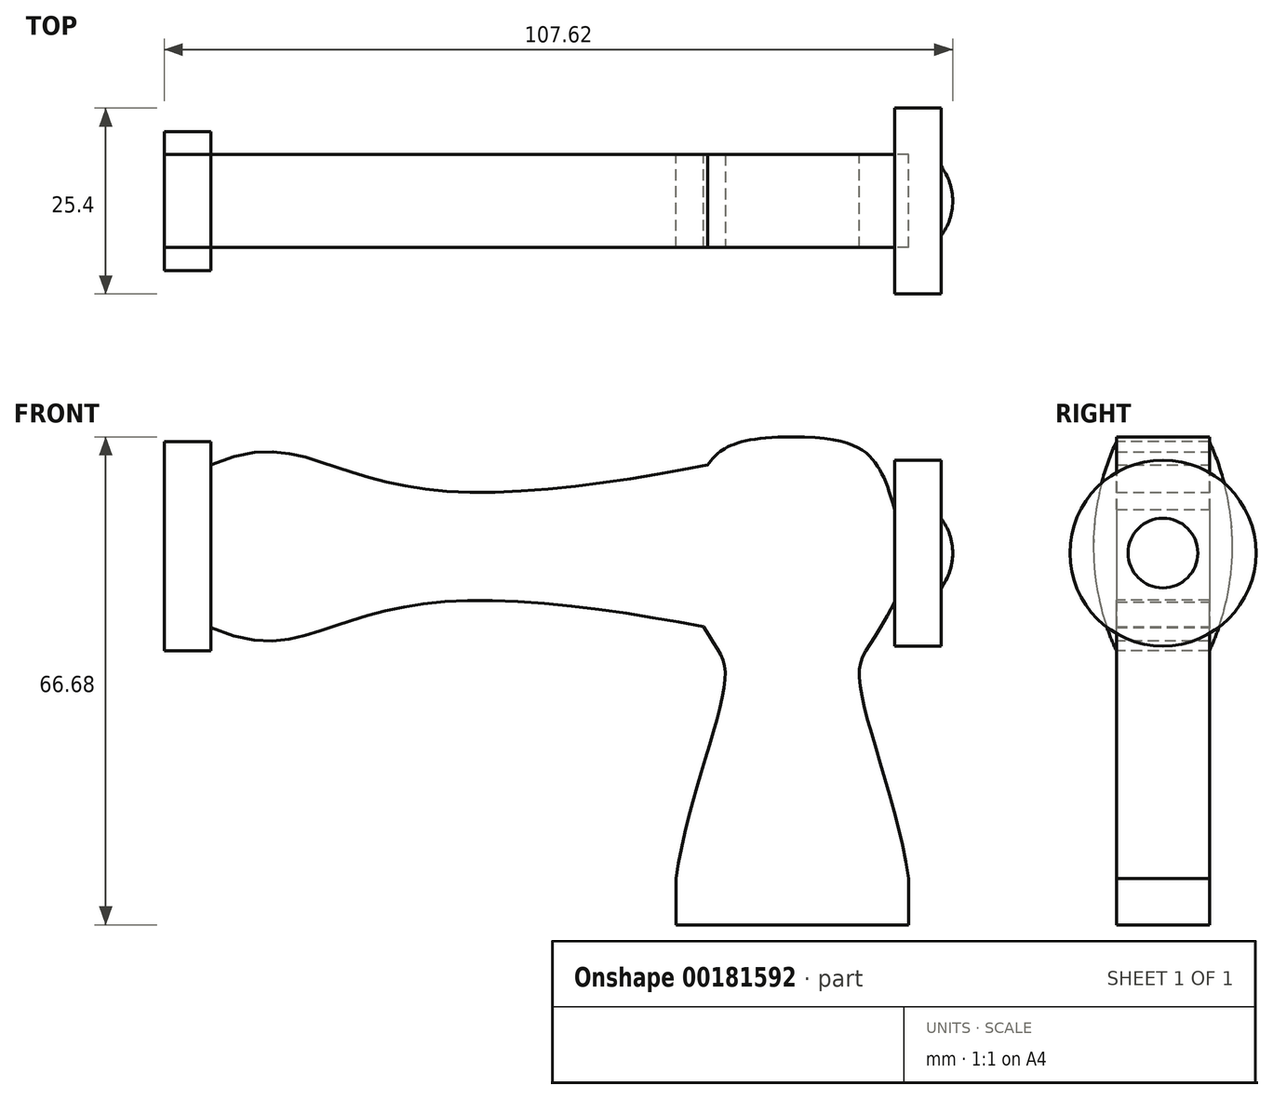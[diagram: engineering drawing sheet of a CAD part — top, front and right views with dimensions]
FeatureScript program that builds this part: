
annotation { "Feature Type Name" : "Feature", "Feature Type Description" : "" }
export const myFeature = defineFeature(function(context is Context, id is Id, definition is map)
    precondition{}
    {
        {
            var Q0;
            Q0=qCreatedBy(makeId("Front.planeOp"),FACE);
            var sketch = newSketch(context, id + "F0", { "sketchPlane" : qUnion([Q0])});
            skLineSegment(sketch, "E0", {"start": v(0, 63.34) * mm, "end": v(0, -25.62) * mm, "construction": true});
            skLineSegment(sketch, "E1", {"start": v(0, 0) * mm, "end": v(15.87, 0) * mm});
            skLineSegment(sketch, "E2", {"start": v(15.88, 0) * mm, "end": v(15.88, 6.35) * mm});
            skFitSpline(sketch, "E3", {"points": [v(15.88, 6.35) * mm, v(9.14, 34) * mm, v(14.67, 45.56) * mm], "startDerivative": vector(-7.68, 53.58) * mm, "endDerivative": vector(26.05, 56.21) * mm});
            skLineSegment(sketch, "E4", {"start": v(14.67, 45.56) * mm, "end": v(14.67, 53.82) * mm});
            skFitSpline(sketch, "E5", {"points": [v(14.67, 53.82) * mm, v(11.53, 62.83) * mm, v(0, 66.68) * mm], "startDerivative": vector(-6.78, 29.85) * mm, "endDerivative": vector(-44.66, 0) * mm});
            skFitSpline(sketch, "E6.MirrorCS", {"points": [v(-14.67, 53.82) * mm, v(-11.53, 62.83) * mm, v(0, 66.68) * mm], "startDerivative": vector(6.78, 29.85) * mm, "endDerivative": vector(44.66, 0) * mm});
            skFitSpline(sketch, "E7.MirrorCS", {"points": [v(-15.87, 6.35) * mm, v(-9.14, 34) * mm, v(-14.67, 45.56) * mm], "startDerivative": vector(7.68, 53.58) * mm, "endDerivative": vector(-26.05, 56.21) * mm});
            skLineSegment(sketch, "E8.MirrorCS", {"start": v(-15.87, 0) * mm, "end": v(-15.87, 6.35) * mm});
            skLineSegment(sketch, "E9.MirrorCS", {"start": v(0, 0) * mm, "end": v(-15.87, 0) * mm});
            skFitSpline(sketch, "E10", {"points": [v(-11.53, 62.83) * mm, v(-45.8, 59.16) * mm, v(-63.17, 62.83) * mm, v(-79.38, 62.83) * mm], "startDerivative": vector(-74.94, -14.82) * mm, "endDerivative": vector(-77.7, -33.1) * mm});
            skLineSegment(sketch, "E11", {"start": v(-90.87, 51.72) * mm, "end": v(5.33, 51.72) * mm, "construction": true});
            skFitSpline(sketch, "E12.MirrorCS", {"points": [v(-11.53, 40.6) * mm, v(-45.8, 44.27) * mm, v(-63.17, 40.6) * mm, v(-79.38, 40.6) * mm], "startDerivative": vector(-74.94, 14.82) * mm, "endDerivative": vector(-77.7, 33.1) * mm});
            skLineSegment(sketch, "E13", {"start": v(-79.38, 62.83) * mm, "end": v(-79.38, 40.6) * mm});
            skSolve(sketch);
        }
        {
            var Q0;
            Q0 = qSketchRegion(id + "F0", true);
            extrude(context, id + "F1", {"entities" : qUnion([Q0]), "depth" : 12.7 * mm});
        }
        {
            var Q0;
            Q0=qCreatedBy(makeId("Front.planeOp"),FACE);
            cPlane(context, id + "F2", {"entities" : qUnion([Q0]), "cplaneType" : CPlaneType.OFFSET, "offset" : 6.35 * mm, "width" : 152.4 * mm, "height" : 152.4 * mm});
        }
        {
            var Q0;
            Q0=qCreatedBy(id+"F2.planeOp",FACE);
            var sketch = newSketch(context, id + "F3", { "sketchPlane" : qUnion([Q0])});
            skLineSegment(sketch, "E14", {"start": v(13.96, 50.8) * mm, "end": v(13.96, 63.5) * mm});
            skLineSegment(sketch, "E15", {"start": v(13.96, 63.5) * mm, "end": v(20.31, 63.5) * mm});
            skLineSegment(sketch, "E16", {"start": v(20.31, 63.5) * mm, "end": v(20.31, 55.56) * mm});
            skArc(sketch, "E17", {"start": v(20.31, 55.56) * mm, "mid": v(21.5, 53.31) * mm, "end": v(21.9, 50.8) * mm});
            skLineSegment(sketch, "E18", {"start": v(13.96, 50.8) * mm, "end": v(21.9, 50.8) * mm});
            skSolve(sketch);
        }
        {
            var Q0;
            Q0 = qSketchRegion(id + "F3", true);
            var Q1;
            Q1=sQuery(id+"F3.wireOp",EDGE,"E18");
            revolve(context, id + "F4", {"operationType" : NewBodyOperationType.ADD, "entities" : qUnion([Q0]), "axis" : qUnion([Q1]), "revolveType" : RevolveType.FULL});
        }
        {
            var Q0;
            Q0=makeQuery(id+"F1.opExtrude","SWEPT_FACE",FACE,{"disambiguationData":[OSD([sQuery(id+"F0.wireOp",EDGE,"E13")])]});
            var sketch = newSketch(context, id + "F5", { "sketchPlane" : qUnion([Q0])});
            skLineSegment(sketch, "E19", {"start": v(6.35, 62.83) * mm, "end": v(6.35, 24.94) * mm, "construction": true});
            skLineSegment(sketch, "E20", {"start": v(6.35, 66) * mm, "end": v(0, 66) * mm});
            skArc(sketch, "E21", {"start": v(0, 66) * mm, "mid": v(-3.14, 51.72) * mm, "end": v(0, 37.43) * mm});
            skLineSegment(sketch, "E22", {"start": v(0, 37.43) * mm, "end": v(6.35, 37.43) * mm});
            skLineSegment(sketch, "E23.MirrorCS", {"start": v(6.35, 66) * mm, "end": v(12.7, 66) * mm});
            skArc(sketch, "E24.MirrorCS", {"start": v(12.7, 66) * mm, "mid": v(15.84, 51.72) * mm, "end": v(12.7, 37.43) * mm});
            skLineSegment(sketch, "E25.MirrorCS", {"start": v(12.7, 37.43) * mm, "end": v(6.35, 37.43) * mm});
            skSolve(sketch);
        }
        {
            var Q0;
            Q0 = qSketchRegion(id + "F5", true);
            extrude(context, id + "F6", {"entities" : qUnion([Q0]), "operationType" : NewBodyOperationType.ADD, "depth" : 6.35 * mm});
        }
    });
